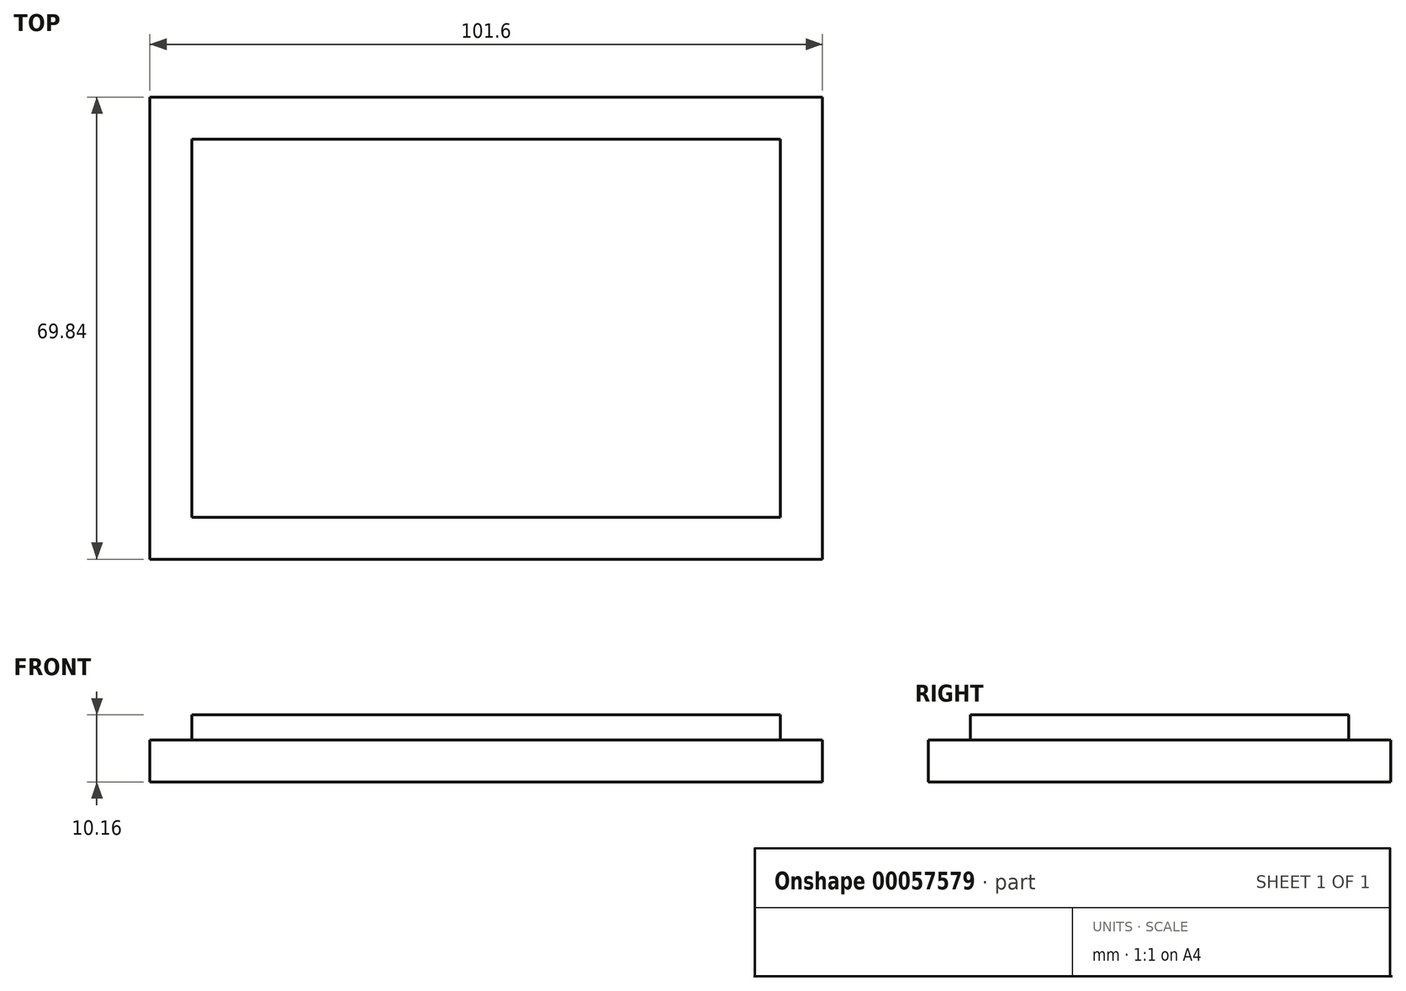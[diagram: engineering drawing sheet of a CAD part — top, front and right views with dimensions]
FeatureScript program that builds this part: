
annotation { "Feature Type Name" : "Feature", "Feature Type Description" : "" }
export const myFeature = defineFeature(function(context is Context, id is Id, definition is map)
    precondition{}
    {
        {
            var Q0;
            Q0=qCreatedBy(makeId("Top.planeOp"),FACE);
            var sketch = newSketch(context, id + "F0", { "sketchPlane" : qUnion([Q0])});
            skLineSegment(sketch, "E0.rect.bottom", {"start": v(50.8, 34.93) * mm, "end": v(-50.8, 34.93) * mm});
            skLineSegment(sketch, "E0.rect.top", {"start": v(50.8, -34.92) * mm, "end": v(-50.8, -34.92) * mm});
            skLineSegment(sketch, "E0.rect.left", {"start": v(50.8, 34.93) * mm, "end": v(50.8, -34.92) * mm});
            skLineSegment(sketch, "E0.rect.right", {"start": v(-50.8, 34.93) * mm, "end": v(-50.8, -34.92) * mm});
            skPoint(sketch, "E0.rect.middle", {"position": v(0, 0) * mm});
            skSolve(sketch);
        }
        {
            var Q0;
            Q0=makeQuery(id+"F0.imprint","IMPRINT",FACE,{"disambiguationData":[TD([[makeQuery(id+"F0.imprint","IMPRINT",EDGE,{"derivedFrom":sQuery(id+"F0.wireOp",EDGE,"E0.rect.bottom")}),1.0]])]});
            extrude(context, id + "F1", {"entities" : qUnion([Q0]), "depth" : 6.35 * mm});
        }
        {
            var Q0;
            Q0=makeQuery(id+"F1.opExtrude","CAP_FACE",FACE,{"disambiguationData":[OSD([sQuery(id+"F0.wireOp",EDGE,"E0.rect.bottom"),sQuery(id+"F0.wireOp",EDGE,"E0.rect.top"),sQuery(id+"F0.wireOp",EDGE,"E0.rect.left"),sQuery(id+"F0.wireOp",EDGE,"E0.rect.right")])],"isStart":false});
            var sketch = newSketch(context, id + "F2", { "sketchPlane" : qUnion([Q0])});
            skLineSegment(sketch, "E1.0", {"start": v(44.45, -28.57) * mm, "end": v(44.45, 28.58) * mm});
            skLineSegment(sketch, "E1.1", {"start": v(-44.45, -28.57) * mm, "end": v(44.45, -28.57) * mm});
            skLineSegment(sketch, "E1.2", {"start": v(-44.45, 28.58) * mm, "end": v(-44.45, -28.57) * mm});
            skLineSegment(sketch, "E1.3", {"start": v(44.45, 28.58) * mm, "end": v(-44.45, 28.58) * mm});
            skSolve(sketch);
        }
        {
            var Q0;
            Q0=makeQuery(id+"F2.imprint","IMPRINT",FACE,{"disambiguationData":[TD([[makeQuery(id+"F2.imprint","IMPRINT",EDGE,{"derivedFrom":sQuery(id+"F2.wireOp",EDGE,"E1.0")}),1.0]])]});
            extrude(context, id + "F3", {"entities" : qUnion([Q0]), "operationType" : NewBodyOperationType.ADD, "depth" : 3.8 * mm});
        }
    });
